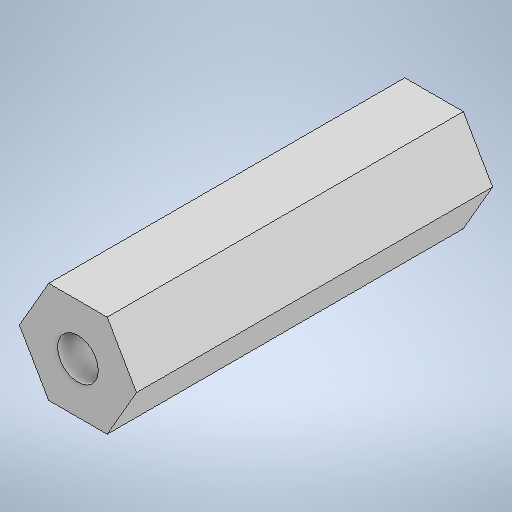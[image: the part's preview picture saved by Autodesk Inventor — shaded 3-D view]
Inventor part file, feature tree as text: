
AUTODESK INVENTOR PART (.ipt)
format: ipt  version: 2025.1 (Build 291241020, 241B)  size: 261,120 bytes
history: native  units: in
note: dims shown in document units (in); Inventor stores cm internally (conversion verified against a paired STEP export)
features: extrude x1, sketch x1
ambient origin geometry x8: Origin, YZ Plane, XZ Plane, XY Plane, X Axis, Y Axis, Z Axis, Center Point
bodies: Solid1 (feature_tree)
feature tree (2):
  extrude  "Extrusion1"  Depth=0.5in
  sketch  "Sketch1"  dims[d0=0.201in d1=0.5in d2=1.756in d3=0.0in]
